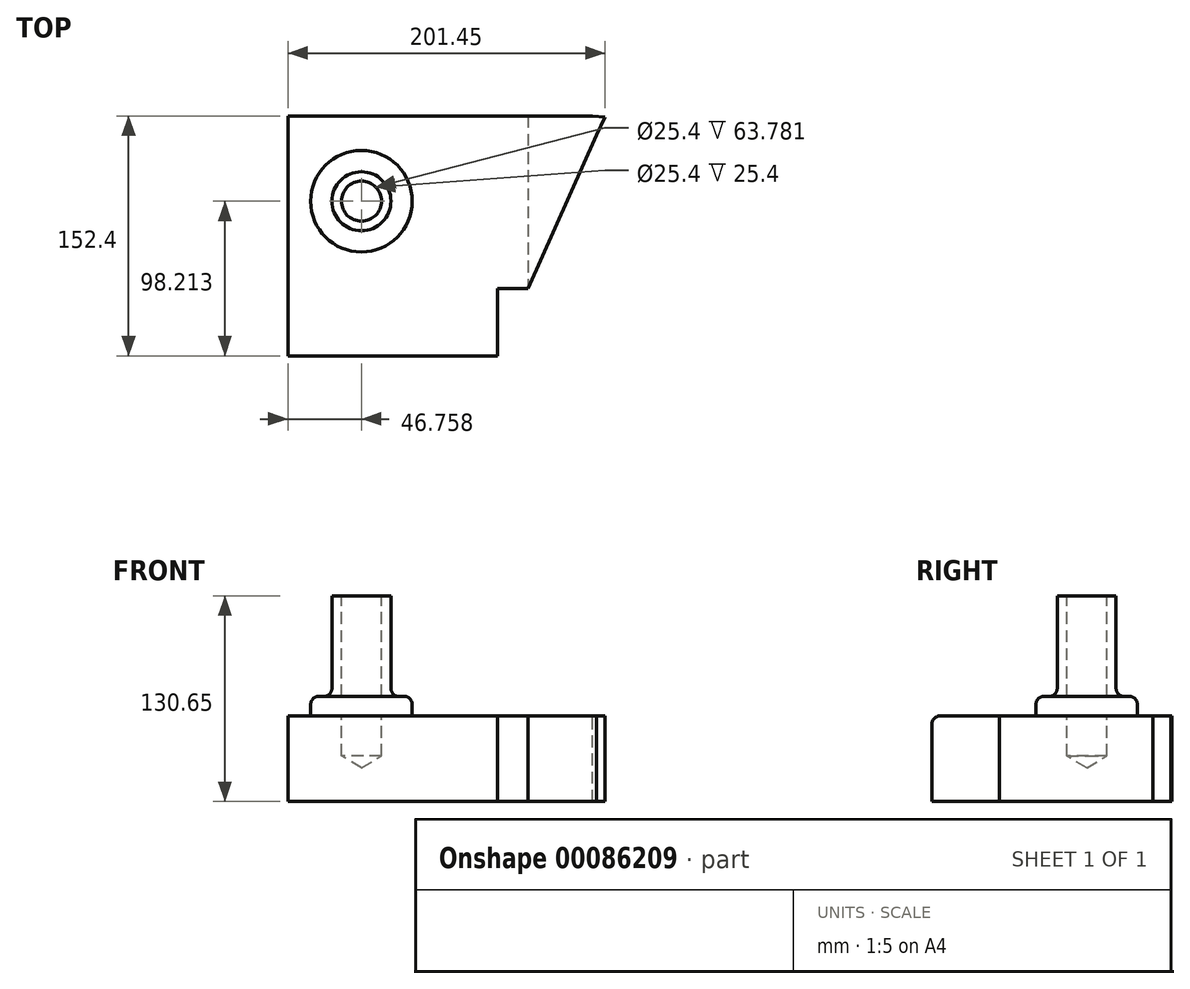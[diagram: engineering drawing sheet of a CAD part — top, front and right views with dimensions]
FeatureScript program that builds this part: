
annotation { "Feature Type Name" : "Feature", "Feature Type Description" : "" }
export const myFeature = defineFeature(function(context is Context, id is Id, definition is map)
    precondition{}
    {
        {
            var Q0;
            Q0=qCreatedBy(makeId("Top.planeOp"),FACE);
            var sketch = newSketch(context, id + "F0", { "sketchPlane" : qUnion([Q0])});
            skLineSegment(sketch, "E0.bottom", {"start": v(43.56, 0.52) * mm, "end": v(221.36, 0.52) * mm});
            skLineSegment(sketch, "E0.top", {"start": v(43.56, -151.88) * mm, "end": v(221.36, -151.88) * mm});
            skLineSegment(sketch, "E0.left", {"start": v(43.56, 0.52) * mm, "end": v(43.56, -151.88) * mm});
            skLineSegment(sketch, "E0.right", {"start": v(221.36, 0.52) * mm, "end": v(221.36, -151.88) * mm});
            skSolve(sketch);
        }
        {
            var Q0;
            Q0=makeQuery(id+"F0.imprint","IMPRINT",FACE,{"disambiguationData":[TD([[makeQuery(id+"F0.imprint","IMPRINT",EDGE,{"derivedFrom":sQuery(id+"F0.wireOp",EDGE,"E0.bottom")}),-1.0]])]});
            extrude(context, id + "F1", {"entities" : qUnion([Q0]), "depth" : 53.97 * mm});
        }
        {
            var Q0;
            Q0=makeQuery(id+"F1.opExtrude","CAP_FACE",FACE,{"disambiguationData":[OSD([sQuery(id+"F0.wireOp",EDGE,"E0.bottom"),sQuery(id+"F0.wireOp",EDGE,"E0.top"),sQuery(id+"F0.wireOp",EDGE,"E0.left"),sQuery(id+"F0.wireOp",EDGE,"E0.right")])],"isStart":false});
            var sketch = newSketch(context, id + "F2", { "sketchPlane" : qUnion([Q0])});
            skLineSegment(sketch, "E1.bottom", {"start": v(176.88, -151.88) * mm, "end": v(221.36, -151.88) * mm});
            skLineSegment(sketch, "E1.top", {"start": v(176.88, -109.18) * mm, "end": v(221.36, -109.18) * mm});
            skLineSegment(sketch, "E1.left", {"start": v(176.88, -151.88) * mm, "end": v(176.88, -109.18) * mm});
            skLineSegment(sketch, "E1.right", {"start": v(221.36, -151.88) * mm, "end": v(221.36, -109.18) * mm});
            skSolve(sketch);
        }
        {
            var Q0;
            Q0=makeQuery(id+"F2.imprint","IMPRINT",FACE,{"disambiguationData":[TD([[makeQuery(id+"F2.imprint","IMPRINT",EDGE,{"derivedFrom":sQuery(id+"F2.wireOp",EDGE,"E1.bottom")}),1.0]])]});
            extrude(context, id + "F3", {"entities" : qUnion([Q0]), "operationType" : NewBodyOperationType.REMOVE, "oppositeDirection" : true, "depth" : 57.3 * mm});
        }
        {
            var Q0;
            Q0=makeQuery(id+"F3.boolean.opBoolean","COPY",EDGE,{"derivedFrom":makeQuery(id+"F3.opExtrude","CAP_EDGE",EDGE,{"disambiguationData":[OSD([sQuery(id+"F2.wireOp",EDGE,"E1.left")])],"isStart":true})});
            var Q1;
            Q1=makeQuery(id+"F1.opExtrude","CAP_EDGE",EDGE,{"disambiguationData":[OSD([sQuery(id+"F0.wireOp",EDGE,"E0.top")])],"isStart":false});
            fillet(context, id + "F4", {"entities" : qUnion([Q0, Q1]), "radius" : 5.08 * mm, "tangentPropagation" : true, "allowEdgeOverflow" : false});
        }
        {
            var Q0;
            Q0=makeQuery(id+"F1.opExtrude","SWEPT_FACE",FACE,{"disambiguationData":[OSD([sQuery(id+"F0.wireOp",EDGE,"E0.right")])]});
            extrude(context, id + "F5", {"entities" : qUnion([Q0]), "operationType" : NewBodyOperationType.REMOVE, "oppositeDirection" : true, "depth" : 25.4 * mm});
        }
        {
            var Q0;
            Q0=makeQuery(id+"F1.opExtrude","CAP_FACE",FACE,{"disambiguationData":[OSD([sQuery(id+"F0.wireOp",EDGE,"E0.bottom"),sQuery(id+"F0.wireOp",EDGE,"E0.top"),sQuery(id+"F0.wireOp",EDGE,"E0.left"),sQuery(id+"F0.wireOp",EDGE,"E0.right")])],"isStart":false});
            var sketch = newSketch(context, id + "F6", { "sketchPlane" : qUnion([Q0])});
            skLineSegment(sketch, "E2", {"start": v(195.96, -109.18) * mm, "end": v(239.56, -11.69) * mm});
            skLineSegment(sketch, "E3", {"start": v(195.96, 0.52) * mm, "end": v(236.98, 0.52) * mm});
            skLineSegment(sketch, "E4", {"start": v(239.56, -11.69) * mm, "end": v(245.01, -0.12) * mm});
            skLineSegment(sketch, "E5", {"start": v(236.98, 0.52) * mm, "end": v(245.01, -0.12) * mm});
            skSolve(sketch);
        }
        {
            var Q0;
            Q0 = qSketchRegion(id + "F6", true);
            var Q1;
            Q1=makeQuery(id+"F6.imprint","IMPRINT",FACE,{"disambiguationData":[TD([[makeQuery(id+"F6.imprint","IMPRINT",EDGE,{"derivedFrom":sQuery(id+"F6.wireOp",EDGE,"E2")}),1.0]])]});
            extrude(context, id + "F7", {"entities" : qUnion([Q0, Q1]), "operationType" : NewBodyOperationType.ADD, "oppositeDirection" : true, "depth" : 53.07 * mm});
        }
        {
            var Q0;
            {var subQ0=sQuery(id+"F0.wireOp",EDGE,"E0.right");Q0=makeQuery(id+"F7.boolean.opBoolean","MERGE",FACE,{"derivedFrom":[makeQuery(id+"F1.opExtrude","CAP_FACE",FACE,{"disambiguationData":[OSD([sQuery(id+"F0.wireOp",EDGE,"E0.bottom"),sQuery(id+"F0.wireOp",EDGE,"E0.top"),sQuery(id+"F0.wireOp",EDGE,"E0.left"),subQ0])],"isStart":false}),makeQuery(id+"F7.opExtrude","CAP_FACE",FACE,{"disambiguationData":[OSD([subQ0,sQuery(id+"F6.wireOp",EDGE,"E2"),sQuery(id+"F6.wireOp",EDGE,"E3"),sQuery(id+"F6.wireOp",EDGE,"E4"),sQuery(id+"F6.wireOp",EDGE,"E5")])],"isStart":true})]});}
            var sketch = newSketch(context, id + "F8", { "sketchPlane" : qUnion([Q0])});
            skCircle(sketch, "E6", {"center": v(90.32, -53.67) * mm, "radius": 18.7 * mm});
            skSolve(sketch);
        }
        {
            var Q0;
            Q0=makeQuery(id+"F8.imprint","IMPRINT",FACE,{"disambiguationData":[TD([[makeQuery(id+"F8.imprint","IMPRINT",EDGE,{"derivedFrom":sQuery(id+"F8.wireOp",EDGE,"E6")}),1.0]])]});
            extrude(context, id + "F9", {"entities" : qUnion([Q0]), "operationType" : NewBodyOperationType.ADD, "depth" : 76.2 * mm});
        }
        {
            var Q0;
            Q0=makeQuery(id+"F9.opExtrude","CAP_FACE",FACE,{"disambiguationData":[OSD([sQuery(id+"F8.wireOp",EDGE,"E6")])],"isStart":false});
            var sketch = newSketch(context, id + "F10", { "sketchPlane" : qUnion([Q0])});
            skCircle(sketch, "E7", {"center": v(90.32, -53.67) * mm, "radius": 14.03 * mm});
            skSolve(sketch);
        }
        {
            var Q0;
            Q0=sQuery(id+"F10.wireOp",VERTEX,"E7.center");
            var Q1;
            Q1=makeQuery(id+"F1.opExtrude","SWEPT_BODY",BODY,{"disambiguationData":[OSD([sQuery(id+"F0.wireOp",EDGE,"E0.bottom"),sQuery(id+"F0.wireOp",EDGE,"E0.top"),sQuery(id+"F0.wireOp",EDGE,"E0.left"),sQuery(id+"F0.wireOp",EDGE,"E0.right")])]});
            hole(context, id + "F11", {"style" : HoleStyle.SIMPLE, "endStyle" : HoleEndStyle.BLIND, "holeDiameter" : 25.4 * mm, "holeDepth" : 101.6 * mm, "locations" : qUnion([Q0]), "scope" : qUnion([Q1])});
        }
        {
            var Q0;
            {var subQ0=sQuery(id+"F0.wireOp",EDGE,"E0.right");Q0=makeQuery(id+"F7.boolean.opBoolean","MERGE",FACE,{"derivedFrom":[makeQuery(id+"F1.opExtrude","CAP_FACE",FACE,{"disambiguationData":[OSD([sQuery(id+"F0.wireOp",EDGE,"E0.bottom"),sQuery(id+"F0.wireOp",EDGE,"E0.top"),sQuery(id+"F0.wireOp",EDGE,"E0.left"),subQ0])],"isStart":false}),makeQuery(id+"F7.opExtrude","CAP_FACE",FACE,{"disambiguationData":[OSD([subQ0,sQuery(id+"F6.wireOp",EDGE,"E2"),sQuery(id+"F6.wireOp",EDGE,"E3"),sQuery(id+"F6.wireOp",EDGE,"E4"),sQuery(id+"F6.wireOp",EDGE,"E5")])],"isStart":true})]});}
            var sketch = newSketch(context, id + "F12", { "sketchPlane" : qUnion([Q0])});
            skCircle(sketch, "E8", {"center": v(90.32, -53.67) * mm, "radius": 32.24 * mm});
            skSolve(sketch);
        }
        {
            var Q0;
            Q0 = qSketchRegion(id + "F12", true);
            extrude(context, id + "F13", {"entities" : qUnion([Q0]), "operationType" : NewBodyOperationType.ADD, "depth" : 12.42 * mm});
        }
        {
            var Q0;
            {var subQ0=sQuery(id+"F12.wireOp",EDGE,"E8");Q0=makeQuery(id+"F13.boolean.opBoolean","SPLIT",FACE,{"disambiguationData":[TD([makeQuery(id+"F9.opExtrude","SWEPT_FACE",FACE,{"disambiguationData":[OSD([sQuery(id+"F8.wireOp",EDGE,"E6")])]})])],"derivedFrom":makeQuery(id+"F13.opExtrude","CAP_FACE",FACE,{"disambiguationData":[OSD([subQ0])],"isStart":false})});}
            fillet(context, id + "F14", {"entities" : qUnion([Q0]), "radius" : 5.08 * mm, "tangentPropagation" : true, "allowEdgeOverflow" : false});
        }
        {
            var Q0;
            Q0=makeQuery(id+"F7.opExtrude","CAP_FACE",FACE,{"disambiguationData":[OSD([sQuery(id+"F0.wireOp",EDGE,"E0.right"),sQuery(id+"F6.wireOp",EDGE,"E2"),sQuery(id+"F6.wireOp",EDGE,"E3"),sQuery(id+"F6.wireOp",EDGE,"E4"),sQuery(id+"F6.wireOp",EDGE,"E5")])],"isStart":false});
            var Q1;
            Q1=makeQuery(id+"F1.opExtrude","CAP_FACE",FACE,{"disambiguationData":[OSD([sQuery(id+"F0.wireOp",EDGE,"E0.bottom"),sQuery(id+"F0.wireOp",EDGE,"E0.top"),sQuery(id+"F0.wireOp",EDGE,"E0.left"),sQuery(id+"F0.wireOp",EDGE,"E0.right")])],"isStart":true});
            extrude(context, id + "F15", {"entities" : qUnion([Q0, Q1]), "operationType" : NewBodyOperationType.ADD, "depth" : 0.3 * mm});
        }
        {
            var Q0;
            Q0=makeQuery(id+"F15.opExtrude","CAP_FACE",FACE,{"disambiguationData":[OSD([sQuery(id+"F0.wireOp",EDGE,"E0.right"),sQuery(id+"F6.wireOp",EDGE,"E2"),sQuery(id+"F6.wireOp",EDGE,"E3"),sQuery(id+"F6.wireOp",EDGE,"E4"),sQuery(id+"F6.wireOp",EDGE,"E5")])],"isStart":false});
            extrude(context, id + "F16", {"entities" : qUnion([Q0]), "operationType" : NewBodyOperationType.ADD, "depth" : 1.07 * mm});
        }
    });
